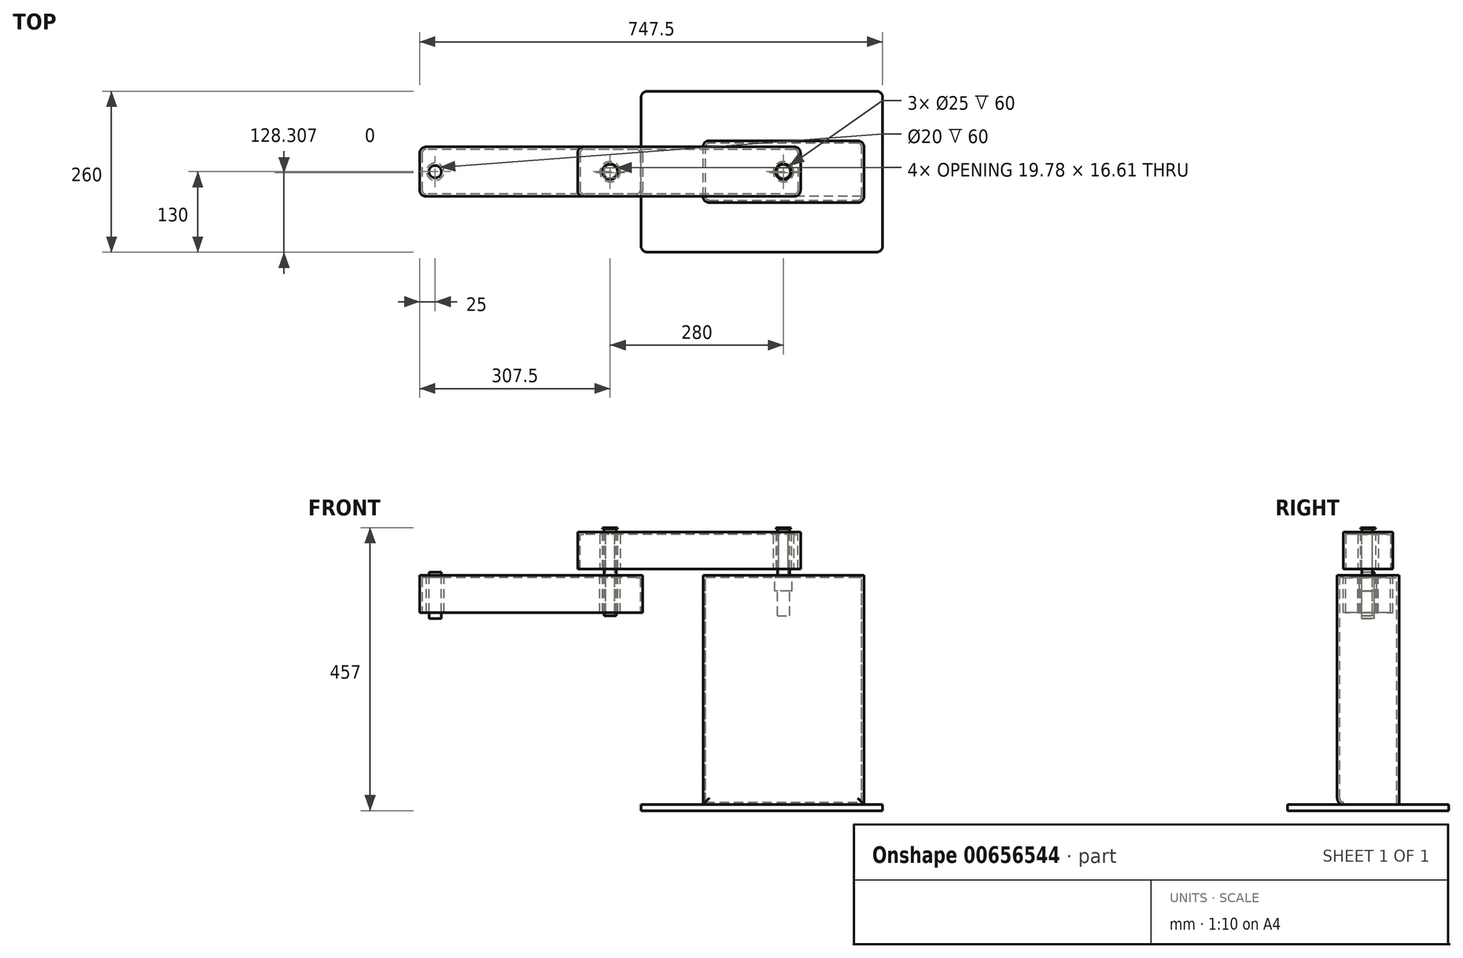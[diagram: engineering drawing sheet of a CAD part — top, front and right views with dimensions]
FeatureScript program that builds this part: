
annotation { "Feature Type Name" : "Feature", "Feature Type Description" : "" }
export const myFeature = defineFeature(function(context is Context, id is Id, definition is map)
    precondition{}
    {
        {
            var Q0;
            Q0=qCreatedBy(makeId("Top.planeOp"),FACE);
            var sketch = newSketch(context, id + "F0", { "sketchPlane" : qUnion([Q0])});
            skLineSegment(sketch, "E0.bottom", {"start": v(180, -40) * mm, "end": v(-180, -40) * mm});
            skLineSegment(sketch, "E0.top", {"start": v(180, 40) * mm, "end": v(-180, 40) * mm});
            skLineSegment(sketch, "E0.left", {"start": v(180, -40) * mm, "end": v(180, 40) * mm});
            skLineSegment(sketch, "E0.right", {"start": v(-180, -40) * mm, "end": v(-180, 40) * mm});
            skPoint(sketch, "E0.middle", {"position": v(0, 0) * mm});
            skCircle(sketch, "E1", {"center": v(-127.5, 0) * mm, "radius": 12.5 * mm});
            skCircle(sketch, "E2", {"center": v(152.5, 0) * mm, "radius": 12.5 * mm});
            skSolve(sketch);
        }
        {
            var Q0;
            Q0=makeQuery(id+"F0.imprint","IMPRINT",FACE,{"disambiguationData":[TD([[makeQuery(id+"F0.imprint","IMPRINT",EDGE,{"derivedFrom":sQuery(id+"F0.wireOp",EDGE,"E0.bottom")}),-1.0]])]});
            extrude(context, id + "F1", {"entities" : qUnion([Q0]), "oppositeDirection" : true, "depth" : 60 * mm, "offsetDistance" : 25 * mm});
        }
        {
            var Q0;
            Q0=makeQuery(id+"F1.opExtrude","CAP_FACE",FACE,{"disambiguationData":[OSD([sQuery(id+"F0.wireOp",EDGE,"E0.bottom"),sQuery(id+"F0.wireOp",EDGE,"E0.top"),sQuery(id+"F0.wireOp",EDGE,"E0.left"),sQuery(id+"F0.wireOp",EDGE,"E0.right"),sQuery(id+"F0.wireOp",EDGE,"E1"),sQuery(id+"F0.wireOp",EDGE,"E2")])],"isStart":true});
            cPlane(context, id + "F2", {"entities" : qUnion([Q0]), "cplaneType" : CPlaneType.OFFSET, "offset" : 10 * mm, "width" : 150 * mm, "height" : 150 * mm});
        }
        {
            var Q0;
            Q0=qCreatedBy(id+"F2.planeOp",FACE);
            var sketch = newSketch(context, id + "F3", { "sketchPlane" : qUnion([Q0])});
            skCircle(sketch, "E3.0", {"center": v(152.5, 0) * mm, "radius": 12.5 * mm, "construction": true});
            skCircle(sketch, "E4.0", {"center": v(-127.5, 0) * mm, "radius": 12.5 * mm});
            skLineSegment(sketch, "E5.bottom", {"start": v(282.5, 50) * mm, "end": v(22.5, 50) * mm});
            skLineSegment(sketch, "E5.top", {"start": v(282.5, -50) * mm, "end": v(22.5, -50) * mm});
            skLineSegment(sketch, "E5.left", {"start": v(282.5, 50) * mm, "end": v(282.5, -50) * mm});
            skLineSegment(sketch, "E5.right", {"start": v(22.5, 50) * mm, "end": v(22.5, -50) * mm});
            skLineSegment(sketch, "E6.bottom", {"start": v(-75, -40) * mm, "end": v(-435, -40) * mm});
            skLineSegment(sketch, "E6.top", {"start": v(-75, 40) * mm, "end": v(-435, 40) * mm});
            skLineSegment(sketch, "E6.left", {"start": v(-75, -40) * mm, "end": v(-75, 40) * mm});
            skLineSegment(sketch, "E6.right", {"start": v(-435, -40) * mm, "end": v(-435, 40) * mm});
            skCircle(sketch, "E7", {"center": v(-410, 0) * mm, "radius": 10 * mm});
            skCircle(sketch, "E8", {"center": v(152.5, 0) * mm, "radius": 10 * mm});
            skSolve(sketch);
        }
        {
            var Q0;
            Q0=makeQuery(id+"F3.imprint","IMPRINT",FACE,{"disambiguationData":[TD([[makeQuery(id+"F3.imprint","IMPRINT",EDGE,{"derivedFrom":sQuery(id+"F3.wireOp",EDGE,"E4.0")}),-1.0]])]});
            extrude(context, id + "F4", {"entities" : qUnion([Q0]), "depth" : 60 * mm, "offsetDistance" : 25 * mm});
        }
        {
            var Q0;
            Q0=makeQuery(id+"F3.imprint","IMPRINT",FACE,{"disambiguationData":[TD([[makeQuery(id+"F3.imprint","IMPRINT",EDGE,{"derivedFrom":sQuery(id+"F3.wireOp",EDGE,"E5.bottom")}),1.0]])]});
            var Q1;
            Q1=makeQuery(id+"F3.imprint","IMPRINT",FACE,{"disambiguationData":[TD([[makeQuery(id+"F3.imprint","IMPRINT",EDGE,{"derivedFrom":sQuery(id+"F3.wireOp",EDGE,"E8")}),1.0]])]});
            extrude(context, id + "F5", {"entities" : qUnion([Q0, Q1]), "depth" : 370 * mm, "offsetDistance" : 25 * mm});
        }
        {
            var Q0;
            Q0=makeQuery(id+"F5.opExtrude","CAP_FACE",FACE,{"disambiguationData":[OSD([sQuery(id+"F3.wireOp",EDGE,"E5.bottom"),sQuery(id+"F3.wireOp",EDGE,"E5.top"),sQuery(id+"F3.wireOp",EDGE,"E5.left"),sQuery(id+"F3.wireOp",EDGE,"E5.right"),sQuery(id+"F3.wireOp",EDGE,"E8")])],"isStart":false});
            var sketch = newSketch(context, id + "F6", { "sketchPlane" : qUnion([Q0])});
            skCircle(sketch, "E9.0", {"center": v(152.5, 0) * mm, "radius": 10 * mm, "construction": true});
            skLineSegment(sketch, "E10.bottom", {"start": v(312.5, 130) * mm, "end": v(-77.5, 130) * mm});
            skLineSegment(sketch, "E10.top", {"start": v(312.5, -130) * mm, "end": v(-77.5, -130) * mm});
            skLineSegment(sketch, "E10.left", {"start": v(312.5, 130) * mm, "end": v(312.5, -130) * mm});
            skLineSegment(sketch, "E10.right", {"start": v(-77.5, 130) * mm, "end": v(-77.5, -130) * mm});
            skSolve(sketch);
        }
        {
            var Q0;
            Q0=makeQuery(id+"F6.imprint","IMPRINT",FACE,{"disambiguationData":[TD([[makeQuery(id+"F6.imprint","IMPRINT",EDGE,{"derivedFrom":sQuery(id+"F6.wireOp",EDGE,"E10.bottom")}),1.0]])]});
            var Q1;
            Q1=makeQuery(id+"F6.imprint","IMPRINT",FACE,{"disambiguationData":[TD([[makeQuery(id+"F6.imprint","IMPRINT",EDGE,{"derivedFrom":makeQuery(id+"F5.opExtrude","CAP_EDGE",EDGE,{"disambiguationData":[OSD([sQuery(id+"F3.wireOp",EDGE,"E5.bottom")])],"isStart":false})}),1.0]])]});
            var Q2;
            Q2=makeQuery(id+"F6.imprint","IMPRINT",FACE,{"disambiguationData":[TD([[makeQuery(id+"F6.imprint","IMPRINT",EDGE,{"derivedFrom":makeQuery(id+"F5.opExtrude","CAP_EDGE",EDGE,{"disambiguationData":[OSD([sQuery(id+"F3.wireOp",EDGE,"E8")])],"isStart":false})}),1.0]])]});
            extrude(context, id + "F7", {"entities" : qUnion([Q0, Q1, Q2]), "depth" : 10 * mm, "offsetDistance" : 25 * mm});
        }
        {
            var Q0;
            Q0=makeQuery(id+"F3.imprint","IMPRINT",FACE,{"disambiguationData":[TD([[makeQuery(id+"F3.imprint","IMPRINT",EDGE,{"derivedFrom":sQuery(id+"F3.wireOp",EDGE,"E8")}),1.0]])]});
            extrude(context, id + "F8", {"entities" : qUnion([Q0]), "operationType" : NewBodyOperationType.REMOVE, "depth" : 25 * mm, "offsetDistance" : 25 * mm});
        }
        {
            var Q0;
            Q0=makeQuery(id+"F4.opExtrude","SWEPT_EDGE",EDGE,{"disambiguationData":[OSD([sQuery(id+"F3.wireOp",EDGE,"E6.top"),sQuery(id+"F3.wireOp",EDGE,"E6.right")])]});
            var Q1;
            Q1=makeQuery(id+"F4.opExtrude","SWEPT_EDGE",EDGE,{"disambiguationData":[OSD([sQuery(id+"F3.wireOp",EDGE,"E6.bottom"),sQuery(id+"F3.wireOp",EDGE,"E6.right")])]});
            var Q2;
            Q2=makeQuery(id+"F4.opExtrude","SWEPT_EDGE",EDGE,{"disambiguationData":[OSD([sQuery(id+"F3.wireOp",EDGE,"E6.bottom"),sQuery(id+"F3.wireOp",EDGE,"E6.left")])]});
            var Q3;
            Q3=makeQuery(id+"F4.opExtrude","SWEPT_EDGE",EDGE,{"disambiguationData":[OSD([sQuery(id+"F3.wireOp",EDGE,"E6.top"),sQuery(id+"F3.wireOp",EDGE,"E6.left")])]});
            var Q4;
            Q4=makeQuery(id+"F1.opExtrude","SWEPT_EDGE",EDGE,{"disambiguationData":[OSD([sQuery(id+"F0.wireOp",EDGE,"E0.bottom"),sQuery(id+"F0.wireOp",EDGE,"E0.left")])]});
            var Q5;
            Q5=makeQuery(id+"F1.opExtrude","SWEPT_EDGE",EDGE,{"disambiguationData":[OSD([sQuery(id+"F0.wireOp",EDGE,"E0.top"),sQuery(id+"F0.wireOp",EDGE,"E0.left")])]});
            var Q6;
            Q6=makeQuery(id+"F1.opExtrude","SWEPT_EDGE",EDGE,{"disambiguationData":[OSD([sQuery(id+"F0.wireOp",EDGE,"E0.bottom"),sQuery(id+"F0.wireOp",EDGE,"E0.right")])]});
            var Q7;
            Q7=makeQuery(id+"F1.opExtrude","SWEPT_EDGE",EDGE,{"disambiguationData":[OSD([sQuery(id+"F0.wireOp",EDGE,"E0.top"),sQuery(id+"F0.wireOp",EDGE,"E0.right")])]});
            var Q8;
            Q8=makeQuery(id+"F5.opExtrude","SWEPT_EDGE",EDGE,{"disambiguationData":[OSD([sQuery(id+"F3.wireOp",EDGE,"E5.bottom"),sQuery(id+"F3.wireOp",EDGE,"E5.right")])]});
            var Q9;
            Q9=makeQuery(id+"F5.opExtrude","SWEPT_EDGE",EDGE,{"disambiguationData":[OSD([sQuery(id+"F3.wireOp",EDGE,"E5.top"),sQuery(id+"F3.wireOp",EDGE,"E5.right")])]});
            var Q10;
            Q10=makeQuery(id+"F5.opExtrude","SWEPT_EDGE",EDGE,{"disambiguationData":[OSD([sQuery(id+"F3.wireOp",EDGE,"E5.bottom"),sQuery(id+"F3.wireOp",EDGE,"E5.left")])]});
            var Q11;
            Q11=makeQuery(id+"F5.opExtrude","SWEPT_EDGE",EDGE,{"disambiguationData":[OSD([sQuery(id+"F3.wireOp",EDGE,"E5.top"),sQuery(id+"F3.wireOp",EDGE,"E5.left")])]});
            var Q12;
            Q12=makeQuery(id+"F7.opExtrude","SWEPT_EDGE",EDGE,{"disambiguationData":[OSD([sQuery(id+"F6.wireOp",EDGE,"E10.bottom"),sQuery(id+"F6.wireOp",EDGE,"E10.right")])]});
            var Q13;
            Q13=makeQuery(id+"F7.opExtrude","SWEPT_EDGE",EDGE,{"disambiguationData":[OSD([sQuery(id+"F6.wireOp",EDGE,"E10.top"),sQuery(id+"F6.wireOp",EDGE,"E10.right")])]});
            var Q14;
            Q14=makeQuery(id+"F7.opExtrude","SWEPT_EDGE",EDGE,{"disambiguationData":[OSD([sQuery(id+"F6.wireOp",EDGE,"E10.top"),sQuery(id+"F6.wireOp",EDGE,"E10.left")])]});
            var Q15;
            Q15=makeQuery(id+"F7.opExtrude","SWEPT_EDGE",EDGE,{"disambiguationData":[OSD([sQuery(id+"F6.wireOp",EDGE,"E10.bottom"),sQuery(id+"F6.wireOp",EDGE,"E10.left")])]});
            var Q16;
            Q16=makeQuery(id+"F5.opExtrude","CAP_EDGE",EDGE,{"disambiguationData":[OSD([sQuery(id+"F3.wireOp",EDGE,"E5.bottom")])],"isStart":false});
            fillet(context, id + "F9", {"entities" : qUnion([Q0, Q1, Q2, Q3, Q4, Q5, Q6, Q7, Q8, Q9, Q10, Q11, Q12, Q13, Q14, Q15, Q16]), "radius" : 10 * mm, "tangentPropagation" : true, "allowEdgeOverflow" : false});
        }
        {
            var Q0;
            Q0=makeQuery(id+"F5.opExtrude","CAP_FACE",FACE,{"disambiguationData":[OSD([sQuery(id+"F3.wireOp",EDGE,"E5.bottom"),sQuery(id+"F3.wireOp",EDGE,"E5.top"),sQuery(id+"F3.wireOp",EDGE,"E5.left"),sQuery(id+"F3.wireOp",EDGE,"E5.right")])],"isStart":false});
            var Q1;
            Q1=makeQuery(id+"F8.boolean.opBoolean","COPY",FACE,{"derivedFrom":makeQuery(id+"F8.opExtrude","CAP_FACE",FACE,{"disambiguationData":[OSD([sQuery(id+"F3.wireOp",EDGE,"E8")])],"isStart":false})});
            var Q2;
            Q2=makeQuery(id+"F1.opExtrude","CAP_FACE",FACE,{"disambiguationData":[OSD([sQuery(id+"F0.wireOp",EDGE,"E0.bottom"),sQuery(id+"F0.wireOp",EDGE,"E0.top"),sQuery(id+"F0.wireOp",EDGE,"E0.left"),sQuery(id+"F0.wireOp",EDGE,"E0.right"),sQuery(id+"F0.wireOp",EDGE,"E1"),sQuery(id+"F0.wireOp",EDGE,"E2")])],"isStart":true});
            var Q3;
            Q3=makeQuery(id+"F4.opExtrude","CAP_FACE",FACE,{"disambiguationData":[OSD([sQuery(id+"F3.wireOp",EDGE,"E4.0"),sQuery(id+"F3.wireOp",EDGE,"E6.bottom"),sQuery(id+"F3.wireOp",EDGE,"E6.top"),sQuery(id+"F3.wireOp",EDGE,"E6.left"),sQuery(id+"F3.wireOp",EDGE,"E6.right"),sQuery(id+"F3.wireOp",EDGE,"E7")])],"isStart":false});
            shell(context, id + "F10", {"entities" : qUnion([Q0, Q1, Q2, Q3]), "thickness" : 4 * mm});
        }
        {
            var Q0;
            Q0=makeQuery(id+"F4.opExtrude","CAP_FACE",FACE,{"disambiguationData":[OSD([sQuery(id+"F3.wireOp",EDGE,"E4.0"),sQuery(id+"F3.wireOp",EDGE,"E6.bottom"),sQuery(id+"F3.wireOp",EDGE,"E6.top"),sQuery(id+"F3.wireOp",EDGE,"E6.left"),sQuery(id+"F3.wireOp",EDGE,"E6.right"),sQuery(id+"F3.wireOp",EDGE,"E7")])],"isStart":true});
            var sketch = newSketch(context, id + "F11", { "sketchPlane" : qUnion([Q0])});
            skCircle(sketch, "E11.0", {"center": v(-410, 0) * mm, "radius": 10 * mm});
            skSolve(sketch);
        }
        {
            var Q0;
            Q0 = qSketchRegion(id + "F11", true);
            extrude(context, id + "F12", {"entities" : qUnion([Q0]), "oppositeDirection" : true, "depth" : 70 * mm, "offsetDistance" : 25 * mm, "hasSecondDirection" : true, "secondDirectionOppositeDirection" : false, "secondDirectionDepth" : 5 * mm});
        }
        {
            var Q0;
            Q0=makeQuery(id+"F1.opExtrude","CAP_FACE",FACE,{"disambiguationData":[OSD([sQuery(id+"F0.wireOp",EDGE,"E0.bottom"),sQuery(id+"F0.wireOp",EDGE,"E0.top"),sQuery(id+"F0.wireOp",EDGE,"E0.left"),sQuery(id+"F0.wireOp",EDGE,"E0.right"),sQuery(id+"F0.wireOp",EDGE,"E1"),sQuery(id+"F0.wireOp",EDGE,"E2")])],"isStart":false});
            var sketch = newSketch(context, id + "F13", { "sketchPlane" : qUnion([Q0])});
            skCircle(sketch, "E12.0", {"center": v(-127.5, 0) * mm, "radius": 12.5 * mm});
            skCircle(sketch, "E13.0", {"center": v(152.5, 0) * mm, "radius": 12.5 * mm});
            skArc(sketch, "E14", {"start": v(-135, 6.61) * mm, "mid": v(-127.5, -10) * mm, "end": v(-120, 6.61) * mm});
            skArc(sketch, "E15", {"start": v(145, 6.61) * mm, "mid": v(152.5, -10) * mm, "end": v(160, 6.61) * mm});
            skLineSegment(sketch, "E16", {"start": v(-135, 6.61) * mm, "end": v(-120, 6.61) * mm});
            skLineSegment(sketch, "E17", {"start": v(145, 6.61) * mm, "end": v(160, 6.61) * mm});
            skSolve(sketch);
        }
        {
            var Q0;
            Q0=makeQuery(id+"F13.imprint","IMPRINT",FACE,{"disambiguationData":[TD([[makeQuery(id+"F13.imprint","IMPRINT",EDGE,{"derivedFrom":sQuery(id+"F13.wireOp",EDGE,"E12.0")}),-1.0]])]});
            var Q1;
            Q1=makeQuery(id+"F13.imprint","IMPRINT",FACE,{"disambiguationData":[TD([[makeQuery(id+"F13.imprint","IMPRINT",EDGE,{"derivedFrom":sQuery(id+"F13.wireOp",EDGE,"E13.0")}),-1.0]])]});
            extrude(context, id + "F14", {"entities" : qUnion([Q0, Q1]), "oppositeDirection" : true, "depth" : 60 * mm, "offsetDistance" : 25 * mm});
        }
        {
            var Q0;
            Q0=makeQuery(id+"F4.opExtrude","CAP_FACE",FACE,{"disambiguationData":[OSD([sQuery(id+"F3.wireOp",EDGE,"E4.0"),sQuery(id+"F3.wireOp",EDGE,"E6.bottom"),sQuery(id+"F3.wireOp",EDGE,"E6.top"),sQuery(id+"F3.wireOp",EDGE,"E6.left"),sQuery(id+"F3.wireOp",EDGE,"E6.right"),sQuery(id+"F3.wireOp",EDGE,"E7")])],"isStart":true});
            var sketch = newSketch(context, id + "F15", { "sketchPlane" : qUnion([Q0])});
            skCircle(sketch, "E18.0", {"center": v(-127.5, 0) * mm, "radius": 12.5 * mm});
            skArc(sketch, "E19.0", {"start": v(-135, 6.61) * mm, "mid": v(-127.5, -10) * mm, "end": v(-120, 6.61) * mm});
            skLineSegment(sketch, "E20.0", {"start": v(-135, 6.61) * mm, "end": v(-120, 6.61) * mm});
            skSolve(sketch);
        }
        {
            var Q0;
            Q0=makeQuery(id+"F15.imprint","IMPRINT",FACE,{"disambiguationData":[TD([[makeQuery(id+"F15.imprint","IMPRINT",EDGE,{"derivedFrom":sQuery(id+"F15.wireOp",EDGE,"E18.0")}),-1.0]])]});
            extrude(context, id + "F16", {"entities" : qUnion([Q0]), "oppositeDirection" : true, "depth" : 60 * mm, "offsetDistance" : 25 * mm});
        }
        {
            var Q0;
            Q0=makeQuery(id+"F13.imprint","IMPRINT",FACE,{"disambiguationData":[TD([[makeQuery(id+"F13.imprint","IMPRINT",EDGE,{"derivedFrom":sQuery(id+"F13.wireOp",EDGE,"E14")}),1.0]])]});
            var Q1;
            Q1=makeQuery(id+"F13.imprint","IMPRINT",FACE,{"disambiguationData":[TD([[makeQuery(id+"F13.imprint","IMPRINT",EDGE,{"derivedFrom":sQuery(id+"F13.wireOp",EDGE,"E15")}),1.0]])]});
            extrude(context, id + "F17", {"entities" : qUnion([Q0, Q1]), "oppositeDirection" : true, "depth" : 135 * mm, "offsetDistance" : 25 * mm, "hasSecondDirection" : true, "secondDirectionOppositeDirection" : false, "secondDirectionDepth" : 5 * mm});
        }
        {
            var Q0;
            Q0=makeQuery(id+"F17.opExtrude","CAP_FACE",FACE,{"disambiguationData":[OSD([sQuery(id+"F13.wireOp",EDGE,"E15"),sQuery(id+"F13.wireOp",EDGE,"E17")])],"isStart":false});
            var sketch = newSketch(context, id + "F18", { "sketchPlane" : qUnion([Q0])});
            skArc(sketch, "E21.0", {"start": v(145, -6.61) * mm, "mid": v(152.5, 10) * mm, "end": v(160, -6.61) * mm, "construction": true});
            skLineSegment(sketch, "E22.0", {"start": v(145, -6.61) * mm, "end": v(160, -6.61) * mm});
            skArc(sketch, "E23", {"start": v(160, -6.61) * mm, "mid": v(152.5, -10) * mm, "end": v(145, -6.61) * mm});
            skSolve(sketch);
        }
        {
            var Q0;
            Q0=makeQuery(id+"F18.imprint","IMPRINT",FACE,{"disambiguationData":[TD([[makeQuery(id+"F18.imprint","IMPRINT",EDGE,{"derivedFrom":sQuery(id+"F18.wireOp",EDGE,"E22.0")}),-1.0]])]});
            extrude(context, id + "F19", {"entities" : qUnion([Q0]), "operationType" : NewBodyOperationType.ADD, "oppositeDirection" : true, "depth" : 65 * mm, "offsetDistance" : 25 * mm});
        }
        {
            var Q0;
            Q0=qCreatedBy(makeId("Front.planeOp"),FACE);
            var sketch = newSketch(context, id + "F20", { "sketchPlane" : qUnion([Q0])});
            skPoint(sketch, "E24.0", {"position": v(-127.5, -65) * mm});
            skLineSegment(sketch, "E25", {"start": v(-127.5, -65) * mm, "end": v(-139.5, -65) * mm});
            skLineSegment(sketch, "E26", {"start": v(-139.5, -65) * mm, "end": v(-139.5, -67) * mm});
            skLineSegment(sketch, "E27", {"start": v(-139.5, -67) * mm, "end": v(-127.5, -67) * mm});
            skLineSegment(sketch, "E28", {"start": v(-127.5, -67) * mm, "end": v(-127.5, -65) * mm});
            skPoint(sketch, "E29.0", {"position": v(152.5, -65) * mm});
            skLineSegment(sketch, "E30", {"start": v(152.5, -65) * mm, "end": v(140.5, -65) * mm});
            skLineSegment(sketch, "E31", {"start": v(140.5, -65) * mm, "end": v(140.5, -67) * mm});
            skLineSegment(sketch, "E32", {"start": v(140.5, -67) * mm, "end": v(152.5, -67) * mm});
            skLineSegment(sketch, "E33", {"start": v(152.5, -67) * mm, "end": v(152.5, -65) * mm});
            skSolve(sketch);
        }
        {
            var Q0;
            Q0=makeQuery(id+"F20.imprint","IMPRINT",FACE,{"disambiguationData":[TD([[makeQuery(id+"F20.imprint","IMPRINT",EDGE,{"derivedFrom":sQuery(id+"F20.wireOp",EDGE,"E30")}),1.0]])]});
            var Q1;
            Q1=sQuery(id+"F20.wireOp",EDGE,"E33");
            revolve(context, id + "F21", {"operationType" : NewBodyOperationType.ADD, "surfaceOperationType" : NewSurfaceOperationType.NEW, "entities" : qUnion([Q0]), "axis" : qUnion([Q1]), "revolveType" : RevolveType.FULL});
        }
        {
            var Q0;
            Q0=makeQuery(id+"F20.imprint","IMPRINT",FACE,{"disambiguationData":[TD([[makeQuery(id+"F20.imprint","IMPRINT",EDGE,{"derivedFrom":sQuery(id+"F20.wireOp",EDGE,"E25")}),1.0]])]});
            var Q1;
            Q1=sQuery(id+"F20.wireOp",EDGE,"E28");
            revolve(context, id + "F22", {"operationType" : NewBodyOperationType.ADD, "surfaceOperationType" : NewSurfaceOperationType.NEW, "entities" : qUnion([Q0]), "axis" : qUnion([Q1]), "revolveType" : RevolveType.FULL});
        }
        {
            var Q0;
            Q0=qCreatedBy(makeId("Front.planeOp"),FACE);
            var sketch = newSketch(context, id + "F23", { "sketchPlane" : qUnion([Q0])});
            skLineSegment(sketch, "E34", {"start": v(0, -206.58) * mm, "end": v(0, 253.91) * mm, "construction": true});
            skLineSegment(sketch, "E35", {"start": v(261.15, -60) * mm, "end": v(-273.03, -60) * mm, "construction": true});
            skSolve(sketch);
        }
        {
            var Q0;
            Q0=makeQuery(id+"F1.opExtrude","SWEPT_BODY",BODY,{"disambiguationData":[OSD([sQuery(id+"F0.wireOp",EDGE,"E0.bottom"),sQuery(id+"F0.wireOp",EDGE,"E0.top"),sQuery(id+"F0.wireOp",EDGE,"E0.left"),sQuery(id+"F0.wireOp",EDGE,"E0.right"),sQuery(id+"F0.wireOp",EDGE,"E1"),sQuery(id+"F0.wireOp",EDGE,"E2")])]});
            var Q1;
            Q1=makeQuery(id+"F5.opExtrude","SWEPT_BODY",BODY,{"disambiguationData":[OSD([sQuery(id+"F3.wireOp",EDGE,"E5.bottom"),sQuery(id+"F3.wireOp",EDGE,"E5.top"),sQuery(id+"F3.wireOp",EDGE,"E5.left"),sQuery(id+"F3.wireOp",EDGE,"E5.right")])]});
            var Q2;
            Q2=makeQuery(id+"F4.opExtrude","SWEPT_BODY",BODY,{"disambiguationData":[OSD([sQuery(id+"F3.wireOp",EDGE,"E4.0"),sQuery(id+"F3.wireOp",EDGE,"E6.bottom"),sQuery(id+"F3.wireOp",EDGE,"E6.top"),sQuery(id+"F3.wireOp",EDGE,"E6.left"),sQuery(id+"F3.wireOp",EDGE,"E6.right"),sQuery(id+"F3.wireOp",EDGE,"E7")])]});
            var Q3;
            Q3=makeQuery(id+"F17.opExtrude","SWEPT_BODY",BODY,{"disambiguationData":[OSD([sQuery(id+"F13.wireOp",EDGE,"E15"),sQuery(id+"F13.wireOp",EDGE,"E17")])]});
            var Q4;
            Q4=makeQuery(id+"F14.opExtrude","SWEPT_BODY",BODY,{"disambiguationData":[OSD([sQuery(id+"F13.wireOp",EDGE,"E13.0"),sQuery(id+"F13.wireOp",EDGE,"E15"),sQuery(id+"F13.wireOp",EDGE,"E17")])]});
            var Q5;
            Q5=makeQuery(id+"F14.opExtrude","SWEPT_BODY",BODY,{"disambiguationData":[OSD([sQuery(id+"F13.wireOp",EDGE,"E12.0"),sQuery(id+"F13.wireOp",EDGE,"E14"),sQuery(id+"F13.wireOp",EDGE,"E16")])]});
            var Q6;
            Q6=makeQuery(id+"F17.opExtrude","SWEPT_BODY",BODY,{"disambiguationData":[OSD([sQuery(id+"F13.wireOp",EDGE,"E14"),sQuery(id+"F13.wireOp",EDGE,"E16")])]});
            var Q7;
            Q7=makeQuery(id+"F16.opExtrude","SWEPT_BODY",BODY,{"disambiguationData":[OSD([sQuery(id+"F15.wireOp",EDGE,"E18.0"),sQuery(id+"F15.wireOp",EDGE,"E19.0"),sQuery(id+"F15.wireOp",EDGE,"E20.0")])]});
            var Q8;
            Q8=makeQuery(id+"F12.opExtrude","SWEPT_BODY",BODY,{"disambiguationData":[OSD([sQuery(id+"F11.wireOp",EDGE,"E11.0")])]});
            var Q9;
            Q9=makeQuery(id+"F7.opExtrude","SWEPT_BODY",BODY,{"disambiguationData":[OSD([sQuery(id+"F6.wireOp",EDGE,"E10.bottom"),sQuery(id+"F6.wireOp",EDGE,"E10.top"),sQuery(id+"F6.wireOp",EDGE,"E10.left"),sQuery(id+"F6.wireOp",EDGE,"E10.right")])]});
            var Q10;
            Q10=sQuery(id+"F23.wireOp",EDGE,"E35");
            transform(context, id + "F24", {"entities" : qUnion([Q0, Q1, Q2, Q3, Q4, Q5, Q6, Q7, Q8, Q9]), "transformType" : TransformType.ROTATION, "transformAxis" : qUnion([Q10]), "angle" : 180 * degree, "makeCopy" : false});
        }
    });
